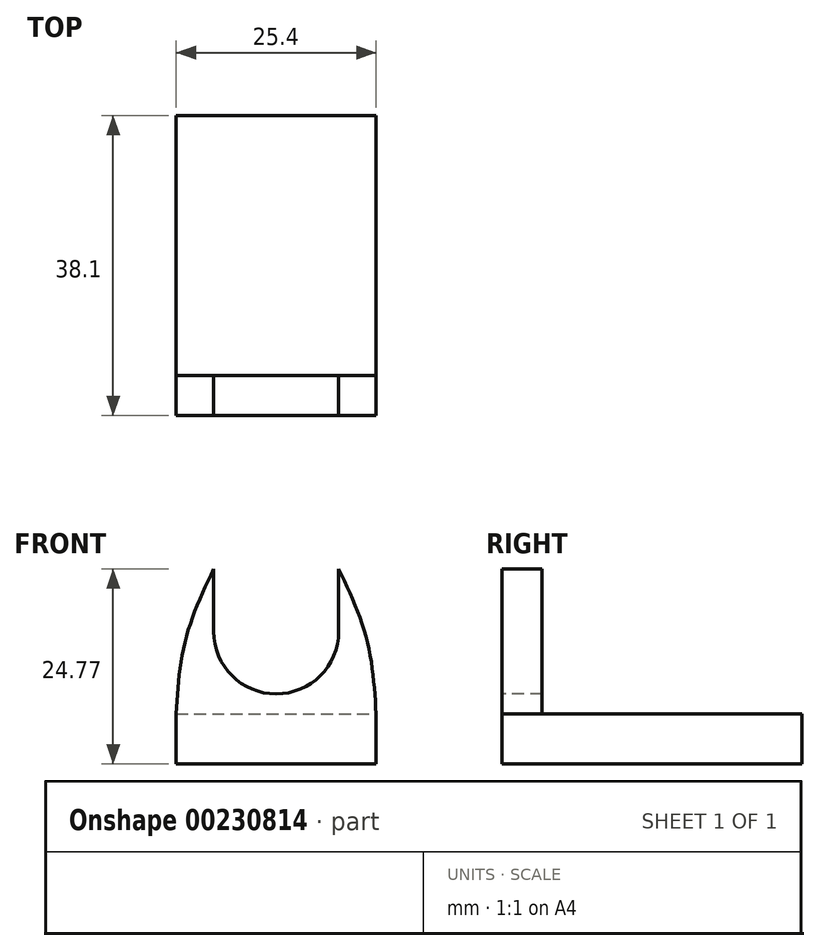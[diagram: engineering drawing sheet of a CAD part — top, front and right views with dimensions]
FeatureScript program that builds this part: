
annotation { "Feature Type Name" : "Feature", "Feature Type Description" : "" }
export const myFeature = defineFeature(function(context is Context, id is Id, definition is map)
    precondition{}
    {
        {
            var Q0;
            Q0=qCreatedBy(makeId("Top.planeOp"),FACE);
            var sketch = newSketch(context, id + "F0", { "sketchPlane" : qUnion([Q0])});
            skLineSegment(sketch, "E0.bottom", {"start": v(0, 0) * mm, "end": v(25.4, 0) * mm});
            skLineSegment(sketch, "E0.top", {"start": v(0, 38.1) * mm, "end": v(25.4, 38.1) * mm});
            skLineSegment(sketch, "E0.left", {"start": v(0, 0) * mm, "end": v(0, 38.1) * mm});
            skLineSegment(sketch, "E0.right", {"start": v(25.4, 0) * mm, "end": v(25.4, 38.1) * mm});
            skSolve(sketch);
        }
        {
            var Q0;
            Q0 = qSketchRegion(id + "F0", true);
            extrude(context, id + "F1", {"entities" : qUnion([Q0]), "depth" : 6.35 * mm});
        }
        {
            var Q0;
            Q0=makeQuery(id+"F1.opExtrude","SWEPT_FACE",FACE,{"disambiguationData":[OSD([sQuery(id+"F0.wireOp",EDGE,"E0.bottom")])]});
            var sketch = newSketch(context, id + "F2", { "sketchPlane" : qUnion([Q0])});
            skLineSegment(sketch, "E1", {"start": v(12.7, 6.35) * mm, "end": v(12.7, 32.4) * mm, "construction": true});
            skCircle(sketch, "E2", {"center": v(12.7, 16.83) * mm, "radius": 7.94 * mm});
            skLineSegment(sketch, "E3", {"start": v(12.7, 16.83) * mm, "end": v(4.76, 16.83) * mm, "construction": true});
            skLineSegment(sketch, "E4", {"start": v(4.76, 16.83) * mm, "end": v(4.76, 24.77) * mm});
            skFitSpline(sketch, "E5", {"points": [v(4.76, 24.77) * mm, v(1.19, 15.78) * mm, v(0, 6.35) * mm], "startDerivative": vector(-8.33, -17.45) * mm, "endDerivative": vector(-1.2, -19.19) * mm});
            skLineSegment(sketch, "E6.MirrorCS", {"start": v(20.64, 16.83) * mm, "end": v(20.64, 24.77) * mm});
            skFitSpline(sketch, "E7.MirrorCS", {"points": [v(20.64, 24.77) * mm, v(24.21, 15.78) * mm, v(25.4, 6.35) * mm], "startDerivative": vector(8.33, -17.45) * mm, "endDerivative": vector(1.2, -19.19) * mm});
            skSolve(sketch);
        }
        {
            var Q0;
            {var subQ0=sQuery(id+"F2.wireOp",EDGE,"E4");Q0=makeQuery(id+"F2.imprint","IMPRINT",FACE,{"disambiguationData":[TD([[makeQuery(id+"F2.imprint","IMPRINT",EDGE,{"derivedFrom":subQ0}),1.0]])]});}
            extrude(context, id + "F3", {"entities" : qUnion([Q0]), "operationType" : NewBodyOperationType.ADD, "oppositeDirection" : true, "depth" : 5.08 * mm});
        }
    });
